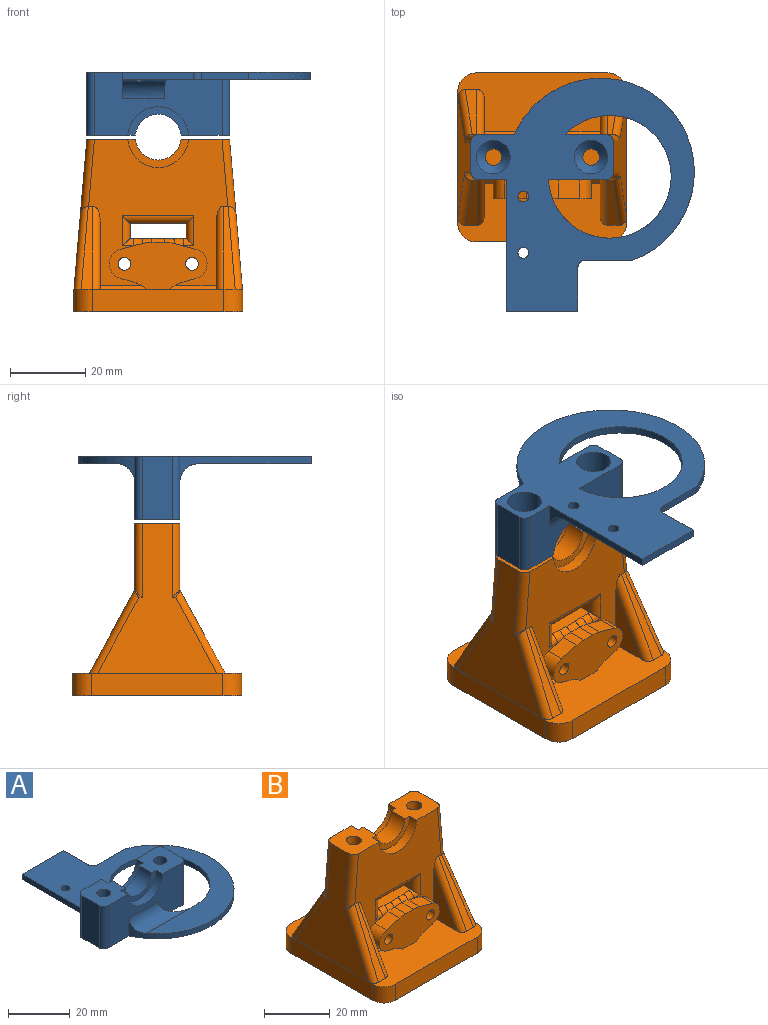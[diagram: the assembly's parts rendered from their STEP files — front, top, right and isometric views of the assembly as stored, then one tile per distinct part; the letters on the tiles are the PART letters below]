
ASSEMBLY  parts=2 mates=2
PART A: 34 faces, bbox 59.5x62x16.8 mm
  f0: plane 62x59.5mm, normal (0,0,-1), area 1639mm2, adj f1,f4,f5,f8,f15,f16,f17,f18
  f1: plane 34x16.8mm, normal (0,-1,0), area 381.4mm2, adj f0,f3,f9,f12,f15,f16,f27,f30
  f2: cylinder r=6.1mm len=12.16mm, axis (0,1,0), area 107.2mm2, adj f3,f9,f11,f13
  f3: plane 12.92x12mm, normal (0,0,1), area 125.9mm2, adj f1,f2,f5,f7,f8,f10,f11,f12
  f4: plane 16.8x8mm, normal (-1,0,0), area 134.4mm2, adj f0,f9,f30,f33
  f5: plane 16.8x8mm, normal (1,0,0), area 134.4mm2, adj f0,f3,f31,f32
  f6: cylinder r=2.2mm len=7.8mm, axis (0,0,-1), area 107.8mm2, adj f9,f26
  f7: cylinder r=2.2mm len=7.8mm, axis (0,0,-1), area 107.8mm2, adj f3,f25
  f8: plane 34x16.8mm, normal (0,1,0), area 398.1mm2, adj f0,f3,f9,f10,f16,f17,f28,f32
  f9: plane 12.92x12mm, normal (0,0,1), area 125.9mm2, adj f1,f2,f4,f6,f8,f10,f11,f12
  f10: cylinder r=8.1mm len=16.17mm, axis (0,1,0), area 74.6mm2, adj f3,f8,f9,f11
  f11: plane 16.17x7.6mm, normal (0,1,0), area 42.6mm2, adj f2,f3,f9,f10
  f12: cylinder r=8.1mm len=16.17mm, axis (0,-1,0), area 74.6mm2, adj f1,f3,f9,f13
  f13: plane 16.17x7.6mm, normal (0,-1,0), area 42.6mm2, adj f2,f3,f9,f12
  f14: plane 62x50mm, normal (0,0,1), area 1181.9mm2, adj f15,f16,f17,f18,f19,f20,f21,f22
  f15: cylinder r=25mm len=48.5mm, axis (0,0,-1), area 203.6mm2, adj f0,f1,f14,f18,f27
  f16: cylinder r=16.34mm len=32.69mm, axis (0,0,-1), area 192.9mm2, adj f0,f1,f8,f14,f27,f28
  f17: plane 35x7mm, normal (-1,0,0), area 75.4mm2, adj f0,f8,f14,f20,f28
  f18: plane 12.53x2mm, normal (0,1,0), area 25.1mm2, adj f0,f14,f15,f29
  f19: plane 11.5x2mm, normal (1,0,0), area 23mm2, adj f0,f14,f20,f29
  f20: plane 19x2mm, normal (0,1,0), area 38mm2, adj f0,f14,f17,f19
  f21: cylinder r=1.45mm len=2.9mm, axis (0,0,-1), area 18.2mm2, adj f0,f14
  f22: cylinder r=1.45mm len=2.9mm, axis (0,0,-1), area 19.3mm2, adj f0,f14,f28
  f23: cylinder r=4.5mm len=9mm, axis (0,0,-1), area 189.4mm2, adj f0,f25
  f24: cylinder r=4.5mm len=9mm, axis (0,0,-1), area 189.4mm2, adj f0,f26
  f25: cone r=2.2mm half-angle=45deg, axis (0,0,-1), area 68.5mm2, adj f7,f23
  f26: cone r=2.2mm half-angle=45deg, axis (0,0,-1), area 68.5mm2, adj f6,f24
  f27: cylinder r=5mm len=23.6mm, axis (1,0,0), area 118.5mm2, adj f1,f14,f15,f16
  f28: cylinder r=5mm len=12.2mm, axis (-1,0,0), area 84.9mm2, adj f8,f14,f16,f17,f22
  f29: cylinder r=2mm len=2mm, axis (0,0,1), area 6.3mm2, adj f0,f14,f18,f19
  f30: cylinder r=2mm len=16.8mm, axis (0,0,-1), area 52.8mm2, adj f0,f1,f4,f9
  f31: cylinder r=2mm len=16.8mm, axis (0,0,1), area 52.8mm2, adj f0,f1,f3,f5
  f32: cylinder r=2mm len=16.8mm, axis (0,0,-1), area 52.8mm2, adj f0,f3,f5,f8
  f33: cylinder r=2mm len=16.8mm, axis (0,0,1), area 52.8mm2, adj f0,f4,f8,f9
PART B: 124 faces, bbox 46.1x46.1x47.3 mm
  f0: plane 7.2x3.84mm, normal (0,0,-1), area 17.2mm2, adj f2,f23,f24,f120
  f1: plane 7.2x3.84mm, normal (0,0,-1), area 17.2mm2, adj f2,f30,f31,f119
  f2: plane 39x37.07mm, normal (0,1,0), area 922.5mm2, adj f0,f1,f7,f16,f17,f21,f23,f24
  f3: plane 39x37.07mm, normal (0,-1,0), area 813.6mm2, adj f7,f16,f19,f39,f40,f41,f43,f44
  f4: cylinder r=2.3mm len=4.6mm, axis (0,0,1), area 44.8mm2, adj f16,f119
  f5: cylinder r=2.3mm len=4.6mm, axis (0,0,1), area 44.8mm2, adj f7,f120
  f6: cylinder r=6.1mm len=12.16mm, axis (0,1,0), area 107.2mm2, adj f7,f16,f18,f20
  f7: plane 12.99x12.07mm, normal (0,0,1), area 124.5mm2, adj f2,f3,f5,f6,f15,f17,f18,f19
  f8: plane 35x6mm, normal (-1,0,0), area 210mm2, adj f12,f13,f101,f104
  f9: plane 35x6mm, normal (0,-1,0), area 210mm2, adj f12,f13,f101,f102
  f10: plane 35x6mm, normal (1,0,0), area 210mm2, adj f12,f13,f102,f103
  f11: plane 35x6mm, normal (0,1,0), area 210mm2, adj f12,f13,f103,f104
  f12: plane 45.46x45.46mm, normal (0,0,1), area 1048.3mm2, adj f8,f9,f10,f11,f14,f15,f46,f63
  f13: plane 45x45mm, normal (0,0,-1), area 2003.5mm2, adj f8,f9,f10,f11,f101,f102,f103,f104
  f14: plane 40x31.82mm, normal (-1,0,0.09), area 580.8mm2, adj f12,f16,f85,f86,f87,f97,f98,f99
  f15: plane 40x31.82mm, normal (1,0,0.09), area 580.8mm2, adj f7,f12,f89,f90,f91,f93,f94,f95
  f16: plane 12.99x12.07mm, normal (0,0,1), area 124.5mm2, adj f2,f3,f4,f6,f14,f17,f18,f19
  f17: cylinder r=8.1mm len=16.17mm, axis (0,1,0), area 74.6mm2, adj f2,f7,f16,f18
  f18: plane 16.17x7.6mm, normal (0,1,0), area 42.6mm2, adj f6,f7,f16,f17
  f19: cylinder r=8.1mm len=16.17mm, axis (0,-1,0), area 74.6mm2, adj f3,f7,f16,f20
  f20: plane 16.17x7.6mm, normal (0,-1,0), area 42.6mm2, adj f6,f7,f16,f19
  f21: plane 10.3x7.2mm, normal (0,0,1), area 48.5mm2, adj f2,f23,f24,f25,f27,f37,f38
  f22: plane 1.54x0.17mm, normal (0,0,-1), area 0.2mm2, adj f25,f37,f38,f120
  f23: plane 8.41x6.21mm, normal (-1,0,0), area 34.4mm2, adj f0,f2,f21,f38,f120
  f24: plane 7.74x5.54mm, normal (1,0,0), area 34.4mm2, adj f0,f2,f21,f37,f120
  f25: plane 4.5x1.2mm, normal (0,1,0), area 5.4mm2, adj f21,f22,f37,f38
  f26: plane 4.6x4.6mm, normal (0,0,1), area 16.6mm2, adj f27
  f27: cylinder r=2.3mm len=5.5mm, axis (0,0,1), area 79.5mm2, adj f21,f26
  f28: plane 10.3x7.2mm, normal (0,0,1), area 48.5mm2, adj f2,f30,f31,f32,f34,f35,f36
  f29: plane 1.54x0.17mm, normal (0,0,-1), area 0.2mm2, adj f32,f35,f36,f119
  f30: plane 8.41x6.21mm, normal (-1,0,0), area 34.4mm2, adj f1,f2,f28,f36,f119
  f31: plane 7.74x5.54mm, normal (1,0,0), area 34.4mm2, adj f1,f2,f28,f35,f119
  f32: plane 4.5x1.2mm, normal (0,1,0), area 5.4mm2, adj f28,f29,f35,f36
  f33: plane 4.6x4.6mm, normal (0,0,1), area 16.6mm2, adj f34
  f34: cylinder r=2.3mm len=5.5mm, axis (0,0,1), area 79.5mm2, adj f28,f33
  f35: plane 5.24x3mm, normal (0.71,0.71,0), area 21.2mm2, adj f28,f29,f31,f32,f119
  f36: plane 5.24x3mm, normal (-0.71,0.71,0), area 21.2mm2, adj f28,f29,f30,f32,f119
  f37: plane 5.24x3mm, normal (0.71,0.71,0), area 21.2mm2, adj f21,f22,f24,f25,f120
  f38: plane 5.24x3mm, normal (-0.71,0.71,0), area 21.2mm2, adj f21,f22,f23,f25,f120
  f39: plane 5x3.08mm, normal (0.26,0,-0.97), area 15.9mm2, adj f3,f46,f69,f70
  f40: cylinder r=4mm len=7.74mm, axis (0,1,0), area 52.6mm2, adj f3,f41,f46,f70
  f41: plane 5.78x5.06mm, normal (0.26,0,0.97), area 29.6mm2, adj f3,f40,f46,f71,f109
  f42: plane 5x3.34mm, normal (0,0,1), area 16.7mm2, adj f46,f71,f72,f113
  f43: plane 5.78x5.06mm, normal (-0.26,0,0.97), area 29.6mm2, adj f3,f44,f46,f72,f117
  f44: cylinder r=4mm len=7.74mm, axis (0,1,0), area 52.6mm2, adj f3,f43,f46,f73
  f45: plane 5x3.08mm, normal (-0.26,0,-0.97), area 15.9mm2, adj f3,f46,f73,f74
  f46: plane 26x12.53mm, normal (0,-1,0), area 228.7mm2, adj f12,f39,f40,f41,f42,f43,f44,f45
  f47: cylinder r=1.7mm len=14mm, axis (0,-1,0), area 149.5mm2, adj f46,f62
  f48: cylinder r=1.7mm len=14mm, axis (0,-1,0), area 149.5mm2, adj f46,f55
  f49: plane 3.29x3mm, normal (1,0,0), area 9.9mm2, adj f2,f50,f54,f55
  f50: plane 3x2.85mm, normal (0.5,0,-0.87), area 9.9mm2, adj f2,f49,f51,f55
  f51: plane 3x2.85mm, normal (-0.5,0,-0.87), area 9.9mm2, adj f2,f50,f52,f55
  f52: plane 3.29x3mm, normal (-1,0,0), area 9.9mm2, adj f2,f51,f53,f55
  f53: plane 3x2.85mm, normal (-0.5,0,0.87), area 9.9mm2, adj f2,f52,f54,f55
  f54: plane 3x2.85mm, normal (0.5,0,0.87), area 9.9mm2, adj f2,f49,f53,f55
  f55: plane 6.58x5.7mm, normal (0,1,0), area 19.1mm2, adj f48,f49,f50,f51,f52,f53,f54
  f56: plane 3x2.85mm, normal (0.5,0,0.87), area 9.9mm2, adj f2,f57,f61,f62
  f57: plane 3.29x3mm, normal (1,0,0), area 9.9mm2, adj f2,f56,f58,f62
  f58: plane 3x2.85mm, normal (0.5,0,-0.87), area 9.9mm2, adj f2,f57,f59,f62
  f59: plane 3x2.85mm, normal (-0.5,0,-0.87), area 9.9mm2, adj f2,f58,f60,f62
  f60: plane 3.29x3mm, normal (-1,0,0), area 9.9mm2, adj f2,f59,f61,f62
  f61: plane 3x2.85mm, normal (-0.5,0,0.87), area 9.9mm2, adj f2,f56,f60,f62
  f62: plane 6.58x5.7mm, normal (0,1,0), area 19.1mm2, adj f47,f56,f57,f58,f59,f60,f61
  f63: plane 18.01x9.82mm, normal (1,0,0), area 87.9mm2, adj f3,f12,f100,f122
  f64: plane 1.89x0.13mm, normal (0,0,1), area 0.2mm2, adj f3,f65,f97,f98,f99,f100
  f65: plane 22x11.99mm, normal (0,-0.88,0.48), area 53.4mm2, adj f12,f64,f97,f100
  f66: plane 1.89x0.13mm, normal (0,0,1), area 0.2mm2, adj f3,f68,f93,f94,f95,f96
  f67: plane 18.01x9.82mm, normal (-1,0,0), area 87.9mm2, adj f3,f12,f96,f121
  f68: plane 22x11.99mm, normal (0,-0.88,0.48), area 53.4mm2, adj f12,f66,f93,f96
  f69: cylinder r=10mm len=5mm, axis (0,1,0), area 21.3mm2, adj f3,f12,f39,f46,f121
  f70: cylinder r=10mm len=5mm, axis (0,1,0), area 0.3mm2, adj f3,f39,f40,f46
  f71: cylinder r=10mm len=5mm, axis (0,1,0), area 13.2mm2, adj f41,f42,f46,f111
  f72: cylinder r=10mm len=5mm, axis (0,1,0), area 13.2mm2, adj f42,f43,f46,f115
  f73: cylinder r=10mm len=5mm, axis (0,1,0), area 0.3mm2, adj f3,f44,f45,f46
  f74: cylinder r=10mm len=5mm, axis (0,-1,0), area 21.3mm2, adj f3,f12,f45,f46,f122
  f75: plane 15x8mm, normal (0,0,-1), area 120mm2, adj f76,f78,f108,f114
  f76: plane 8x4mm, normal (1,0,0), area 32mm2, adj f75,f77,f107,f116
  f77: plane 15x8.27mm, normal (0,0,1), area 122.1mm2, adj f76,f78,f105,f109,f110,f111,f113,f115
  f78: plane 8x4mm, normal (-1,0,0), area 32mm2, adj f75,f77,f106,f112
  f79: plane 18.01x9.82mm, normal (-1,0,0), area 87.9mm2, adj f2,f12,f92,f123
  f80: plane 1.89x0.13mm, normal (0,0,1), area 0.2mm2, adj f2,f81,f89,f90,f91,f92
  f81: plane 22x11.99mm, normal (0,0.88,0.48), area 53.4mm2, adj f12,f80,f89,f92
  f82: plane 18.01x9.82mm, normal (1,0,0), area 87.9mm2, adj f2,f12,f88,f123
  f83: plane 1.89x0.13mm, normal (0,0,1), area 0.2mm2, adj f2,f84,f85,f86,f87,f88
  f84: plane 22x11.99mm, normal (0,0.88,0.48), area 53.4mm2, adj f12,f83,f85,f88
  f85: cylinder r=2mm len=22.81mm, axis (-0.08,0.48,-0.88), area 74.7mm2, adj f12,f14,f83,f84,f87
  f86: cylinder r=2mm len=20.17mm, axis (-0.09,0,-1), area 58.8mm2, adj f2,f14,f16,f83,f87
  f87: cylinder r=2mm len=2.1mm, axis (0,-1,0), area 1.2mm2, adj f14,f83,f85,f86
  f88: cylinder r=2mm len=23mm, axis (0,-0.48,0.88), area 73.4mm2, adj f2,f12,f82,f83,f84
  f89: cylinder r=2mm len=22.81mm, axis (0.08,0.48,-0.88), area 74.7mm2, adj f12,f15,f80,f81,f91
  f90: cylinder r=2mm len=20.17mm, axis (0.09,0,-1), area 58.8mm2, adj f2,f7,f15,f80,f91
  f91: cylinder r=2mm len=2.1mm, axis (0,1,0), area 1.2mm2, adj f15,f80,f89,f90
  f92: cylinder r=2mm len=23mm, axis (0,0.48,-0.88), area 73.4mm2, adj f2,f12,f79,f80,f81
  f93: cylinder r=2mm len=22.81mm, axis (0.08,-0.48,-0.88), area 74.7mm2, adj f12,f15,f66,f68,f95
  f94: cylinder r=2mm len=20.17mm, axis (-0.09,0,1), area 58.8mm2, adj f3,f7,f15,f66,f95
  f95: cylinder r=2mm len=2.1mm, axis (0,1,0), area 1.2mm2, adj f15,f66,f93,f94
  f96: cylinder r=2mm len=23mm, axis (0,0.48,0.88), area 73.4mm2, adj f3,f12,f66,f67,f68
  f97: cylinder r=2mm len=22.81mm, axis (-0.08,-0.48,-0.88), area 74.7mm2, adj f12,f14,f64,f65,f99
  f98: cylinder r=2mm len=20.17mm, axis (0.09,0,1), area 58.8mm2, adj f3,f14,f16,f64,f99
  f99: cylinder r=2mm len=2.1mm, axis (0,-1,0), area 1.2mm2, adj f14,f64,f97,f98
  f100: cylinder r=2mm len=23mm, axis (0,-0.48,-0.88), area 73.4mm2, adj f3,f12,f63,f64,f65
  f101: cylinder r=5mm len=6mm, axis (0,0,-1), area 47.1mm2, adj f8,f9,f12,f13
  f102: cylinder r=5mm len=6mm, axis (0,0,1), area 47.1mm2, adj f9,f10,f12,f13
  f103: cylinder r=5mm len=6mm, axis (0,0,-1), area 47.1mm2, adj f10,f11,f12,f13
  f104: cylinder r=5mm len=6mm, axis (0,0,1), area 47.1mm2, adj f8,f11,f12,f13
  f105: cylinder r=2mm len=19mm, axis (1,0,0), area 53.4mm2, adj f2,f77,f106,f107
  f106: cylinder r=2mm len=8mm, axis (0,0,1), area 18.8mm2, adj f2,f78,f105,f108
  f107: cylinder r=2mm len=8mm, axis (0,0,-1), area 18.8mm2, adj f2,f76,f105,f108
  f108: cylinder r=2mm len=19mm, axis (-1,0,0), area 53.4mm2, adj f2,f75,f106,f107
  f109: bspline ~2.59x2mm, area 7mm2, adj f41,f77,f110,f111
  f110: cylinder r=2mm len=2.8mm, axis (1,0,0), area 4.8mm2, adj f3,f77,f109,f112
  f111: bspline ~4.34x1.97mm, area 5.6mm2, adj f71,f77,f109,f113
  f112: cylinder r=2mm len=8mm, axis (0,0,1), area 18.8mm2, adj f3,f78,f110,f114
  f113: cylinder r=2mm len=3.34mm, axis (1,0,0), area 7mm2, adj f42,f77,f111,f115
  f114: cylinder r=2mm len=19mm, axis (-1,0,0), area 53.4mm2, adj f3,f75,f112,f116
  f115: bspline ~3.71x1.96mm, area 5.6mm2, adj f72,f77,f113,f117
  f116: cylinder r=2mm len=8mm, axis (0,0,-1), area 18.8mm2, adj f3,f76,f114,f118
  f117: bspline ~2.59x2mm, area 7mm2, adj f43,f77,f115,f118
  f118: cylinder r=2mm len=2.8mm, axis (1,0,0), area 4.8mm2, adj f3,f77,f116,f117
  f119: cone r=4.2mm half-angle=45deg, axis (0,0,-1), area 45.7mm2, adj f1,f4,f29,f30,f31,f35,f36
  f120: cone r=4.2mm half-angle=45deg, axis (0,0,-1), area 45.7mm2, adj f0,f5,f22,f23,f24,f37,f38
  f121: plane 12.49x1.06mm, normal (0,-0.71,0.71), area 16.6mm2, adj f3,f12,f67,f69
  f122: plane 12.49x1.06mm, normal (0,-0.71,0.71), area 16.6mm2, adj f3,f12,f63,f74
  f123: plane 30.86x1mm, normal (0,0.71,0.71), area 43.6mm2, adj f2,f12,f79,f82
PLACE A rot(axis=(1,0,0),180deg) t=(-2.08,17.14,67.93)mm
PLACE B t=(-2.08,17.14,4.13)mm
MATE cylindrical A.f7 <-> B.f5  axis (0,0,-1) through (10.92,17.14,51.13)mm
MATE cylindrical A.f6 <-> B.f4  axis (0,0,-1) through (-15.08,17.14,51.13)mm
